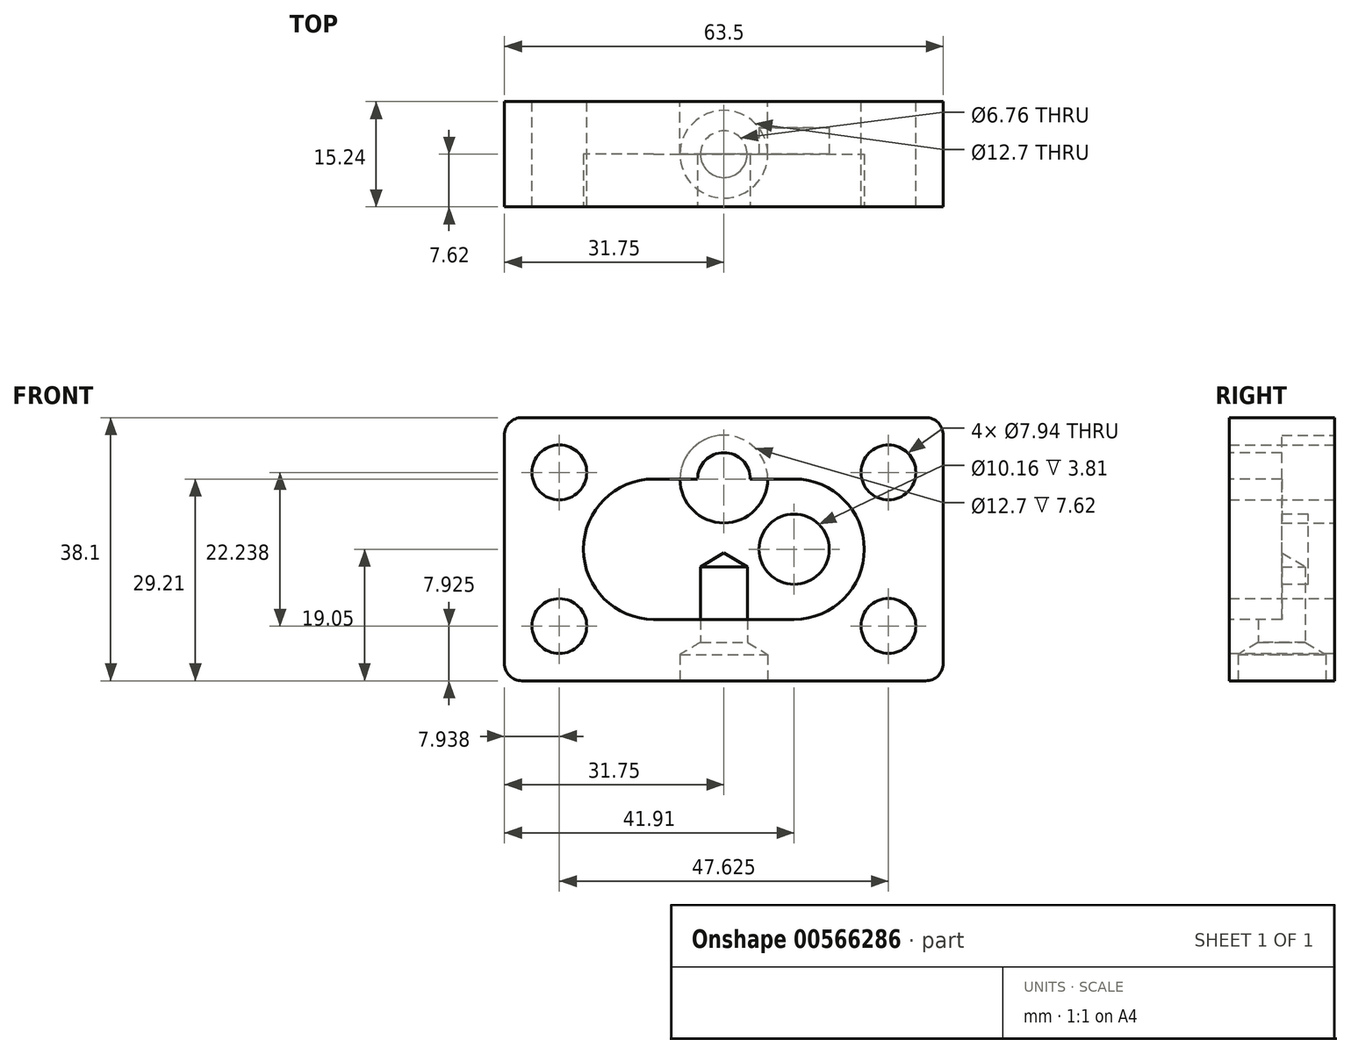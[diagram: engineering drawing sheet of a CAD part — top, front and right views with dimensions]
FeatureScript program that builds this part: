
annotation { "Feature Type Name" : "Feature", "Feature Type Description" : "" }
export const myFeature = defineFeature(function(context is Context, id is Id, definition is map)
    precondition{}
    {
        {
            var Q0;
            Q0=qCreatedBy(makeId("Front.planeOp"),FACE);
            var sketch = newSketch(context, id + "F0", { "sketchPlane" : qUnion([Q0])});
            skLineSegment(sketch, "E0.bottom", {"start": v(-31.75, 19.05) * mm, "end": v(31.75, 19.05) * mm});
            skLineSegment(sketch, "E0.top", {"start": v(-31.75, -19.05) * mm, "end": v(31.75, -19.05) * mm});
            skLineSegment(sketch, "E0.left", {"start": v(-31.75, 19.05) * mm, "end": v(-31.75, -19.05) * mm});
            skLineSegment(sketch, "E0.right", {"start": v(31.75, 19.05) * mm, "end": v(31.75, -19.05) * mm});
            skCircle(sketch, "E1", {"center": v(-23.81, 11.11) * mm, "radius": 3.97 * mm});
            skCircle(sketch, "E2", {"center": v(23.81, 11.11) * mm, "radius": 3.97 * mm});
            skCircle(sketch, "E3", {"center": v(23.81, -11.11) * mm, "radius": 3.97 * mm});
            skCircle(sketch, "E4", {"center": v(-23.81, -11.13) * mm, "radius": 3.97 * mm});
            skSolve(sketch);
        }
        {
            var Q0;
            Q0 = qSketchRegion(id + "F0", true);
            extrude(context, id + "F1", {"entities" : qUnion([Q0]), "depth" : 15.24 * mm, "offsetDistance" : 25.4 * mm});
        }
        {
            var Q0;
            Q0=makeQuery(id+"F1.opExtrude","CAP_FACE",FACE,{"disambiguationData":[OSD([sQuery(id+"F0.wireOp",EDGE,"E0.bottom"),sQuery(id+"F0.wireOp",EDGE,"E0.top"),sQuery(id+"F0.wireOp",EDGE,"E0.left"),sQuery(id+"F0.wireOp",EDGE,"E0.right"),sQuery(id+"F0.wireOp",EDGE,"E1"),sQuery(id+"F0.wireOp",EDGE,"E2"),sQuery(id+"F0.wireOp",EDGE,"E3"),sQuery(id+"F0.wireOp",EDGE,"E4")])],"isStart":false});
            var sketch = newSketch(context, id + "F2", { "sketchPlane" : qUnion([Q0])});
            skCircle(sketch, "E5", {"center": v(10.16, 0) * mm, "radius": 10.16 * mm});
            skCircle(sketch, "E6", {"center": v(-10.16, 0) * mm, "radius": 10.16 * mm});
            skLineSegment(sketch, "E7", {"start": v(-10.16, 10.16) * mm, "end": v(10.16, 10.16) * mm});
            skLineSegment(sketch, "E8", {"start": v(-10.16, -10.16) * mm, "end": v(10.16, -10.16) * mm});
            skSolve(sketch);
        }
        {
            var Q0;
            Q0 = qSketchRegion(id + "F2", true);
            extrude(context, id + "F3", {"entities" : qUnion([Q0]), "operationType" : NewBodyOperationType.REMOVE, "oppositeDirection" : true, "depth" : 7.62 * mm, "offsetDistance" : 25.4 * mm});
        }
        {
            var Q0;
            Q0=makeQuery(id+"F3.boolean.opBoolean","COPY",FACE,{"derivedFrom":makeQuery(id+"F3.opExtrude","CAP_FACE",FACE,{"disambiguationData":[OSD([sQuery(id+"F2.wireOp",EDGE,"E5"),sQuery(id+"F2.wireOp",EDGE,"E6"),sQuery(id+"F2.wireOp",EDGE,"E7"),sQuery(id+"F2.wireOp",EDGE,"E8")])],"isStart":false})});
            var sketch = newSketch(context, id + "F4", { "sketchPlane" : qUnion([Q0])});
            skCircle(sketch, "E9", {"center": v(10.16, 0) * mm, "radius": 5.08 * mm});
            skSolve(sketch);
        }
        {
            var Q0;
            Q0=makeQuery(id+"F4.imprint","IMPRINT",FACE,{"disambiguationData":[TD([[makeQuery(id+"F4.imprint","IMPRINT",EDGE,{"derivedFrom":sQuery(id+"F4.wireOp",EDGE,"E9")}),1.0]])]});
            extrude(context, id + "F5", {"entities" : qUnion([Q0]), "operationType" : NewBodyOperationType.REMOVE, "oppositeDirection" : true, "depth" : 3.8 * mm, "offsetDistance" : 25.4 * mm});
        }
        {
            var Q0;
            Q0=makeQuery(id+"F1.opExtrude","CAP_FACE",FACE,{"disambiguationData":[OSD([sQuery(id+"F0.wireOp",EDGE,"E0.bottom"),sQuery(id+"F0.wireOp",EDGE,"E0.top"),sQuery(id+"F0.wireOp",EDGE,"E0.left"),sQuery(id+"F0.wireOp",EDGE,"E0.right"),sQuery(id+"F0.wireOp",EDGE,"E1"),sQuery(id+"F0.wireOp",EDGE,"E2"),sQuery(id+"F0.wireOp",EDGE,"E3"),sQuery(id+"F0.wireOp",EDGE,"E4")])],"isStart":false});
            var sketch = newSketch(context, id + "F6", { "sketchPlane" : qUnion([Q0])});
            skCircle(sketch, "E10", {"center": v(0, 10.16) * mm, "radius": 3.81 * mm});
            skSolve(sketch);
        }
        {
            var Q0;
            {var subQ0=sQuery(id+"F6.wireOp",EDGE,"E10");var subQ1=makeQuery(id+"F3.boolean.opBoolean","COPY",EDGE,{"derivedFrom":makeQuery(id+"F3.opExtrude","CAP_EDGE",EDGE,{"disambiguationData":[OSD([sQuery(id+"F2.wireOp",EDGE,"E7")])],"isStart":true})});var subQ2=makeQuery(id+"F6.imprint","INTERSECT",VERTEX,{"disambiguationData":[OD(0.0)],"derivedFrom":[subQ1,subQ0]});Q0=makeQuery(id+"F6.imprint","IMPRINT",FACE,{"disambiguationData":[TD([[makeQuery(id+"F6.imprint","IMPRINT",EDGE,{"disambiguationData":[TD([[subQ2,-1.0]])],"derivedFrom":subQ0}),1.0]])]});}
            var Q1;
            {var subQ0=sQuery(id+"F6.wireOp",EDGE,"E10");var subQ1=makeQuery(id+"F3.boolean.opBoolean","COPY",EDGE,{"derivedFrom":makeQuery(id+"F3.opExtrude","CAP_EDGE",EDGE,{"disambiguationData":[OSD([sQuery(id+"F2.wireOp",EDGE,"E7")])],"isStart":true})});var subQ2=makeQuery(id+"F6.imprint","INTERSECT",VERTEX,{"disambiguationData":[OD(0.0)],"derivedFrom":[subQ1,subQ0]});Q1=makeQuery(id+"F6.imprint","IMPRINT",FACE,{"disambiguationData":[TD([[makeQuery(id+"F6.imprint","IMPRINT",EDGE,{"disambiguationData":[TD([[subQ2,1.0]])],"derivedFrom":subQ0}),1.0]])]});}
            extrude(context, id + "F7", {"entities" : qUnion([Q0, Q1]), "operationType" : NewBodyOperationType.REMOVE, "oppositeDirection" : true, "depth" : 25.4 * mm, "offsetDistance" : 25.4 * mm});
        }
        {
            var Q0;
            Q0=makeQuery(id+"F1.opExtrude","CAP_FACE",FACE,{"disambiguationData":[OSD([sQuery(id+"F0.wireOp",EDGE,"E0.bottom"),sQuery(id+"F0.wireOp",EDGE,"E0.top"),sQuery(id+"F0.wireOp",EDGE,"E0.left"),sQuery(id+"F0.wireOp",EDGE,"E0.right"),sQuery(id+"F0.wireOp",EDGE,"E1"),sQuery(id+"F0.wireOp",EDGE,"E2"),sQuery(id+"F0.wireOp",EDGE,"E3"),sQuery(id+"F0.wireOp",EDGE,"E4")])],"isStart":true});
            var sketch = newSketch(context, id + "F8", { "sketchPlane" : qUnion([Q0])});
            skCircle(sketch, "E11", {"center": v(0, 10.16) * mm, "radius": 6.35 * mm});
            skSolve(sketch);
        }
        {
            var Q0;
            Q0=makeQuery(id+"F8.imprint","IMPRINT",FACE,{"disambiguationData":[TD([[makeQuery(id+"F8.imprint","IMPRINT",EDGE,{"derivedFrom":sQuery(id+"F8.wireOp",EDGE,"E11")}),1.0]])]});
            extrude(context, id + "F9", {"entities" : qUnion([Q0]), "operationType" : NewBodyOperationType.REMOVE, "oppositeDirection" : true, "depth" : 7.62 * mm, "offsetDistance" : 25.4 * mm});
        }
        {
            var Q0;
            Q0=makeQuery(id+"F1.opExtrude","SWEPT_FACE",FACE,{"disambiguationData":[OSD([sQuery(id+"F0.wireOp",EDGE,"E0.top")])]});
            var sketch = newSketch(context, id + "F10", { "sketchPlane" : qUnion([Q0])});
            skPoint(sketch, "E12", {"position": v(0, 7.62) * mm});
            skSolve(sketch);
        }
        {
            var Q0;
            Q0=sQuery(id+"F10.wireOp",VERTEX,"E12");
            var Q1;
            Q1=makeQuery(id+"F1.opExtrude","SWEPT_BODY",BODY,{"disambiguationData":[OSD([sQuery(id+"F0.wireOp",EDGE,"E0.bottom"),sQuery(id+"F0.wireOp",EDGE,"E0.top"),sQuery(id+"F0.wireOp",EDGE,"E0.left"),sQuery(id+"F0.wireOp",EDGE,"E0.right"),sQuery(id+"F0.wireOp",EDGE,"E1"),sQuery(id+"F0.wireOp",EDGE,"E2"),sQuery(id+"F0.wireOp",EDGE,"E3"),sQuery(id+"F0.wireOp",EDGE,"E4")])]});
            hole(context, id + "F11", {"style" : HoleStyle.SIMPLE, "endStyle" : HoleEndStyle.BLIND, "standardTappedOrClearance" : lookupTablePath({ "standard" : "ANSI", "fit" : "Normal (ASME)", "engagement" : "75%", "pitch" : "20 tpi", "size" : "1/4", "type" : "Clearance" }), "standardBlindInLast" : lookupTablePath({ "fit" : "Free", "standard" : "ANSI", "engagement" : "75%", "pitch" : "20 tpi", "size" : "1/4", "type" : "Clearance" }), "holeDiameter" : 6.76 * mm, "showTappedDepth" : true, "holeDepth" : 16.51 * mm, "isTappedThrough" : true, "tappedDepth" : 12.7 * mm, "tapClearance" : 3, "locations" : qUnion([Q0]), "scope" : qUnion([Q1]), "majorDiameter" : 6.35 * mm});
        }
        {
            var Q0;
            Q0=makeQuery(id+"F1.opExtrude","SWEPT_FACE",FACE,{"disambiguationData":[OSD([sQuery(id+"F0.wireOp",EDGE,"E0.top")])]});
            var sketch = newSketch(context, id + "F12", { "sketchPlane" : qUnion([Q0])});
            skPoint(sketch, "E13", {"position": v(0, 7.62) * mm});
            skSolve(sketch);
        }
        {
            var Q0;
            Q0=sQuery(id+"F12.wireOp",VERTEX,"E13");
            var Q1;
            Q1=makeQuery(id+"F1.opExtrude","SWEPT_BODY",BODY,{"disambiguationData":[OSD([sQuery(id+"F0.wireOp",EDGE,"E0.bottom"),sQuery(id+"F0.wireOp",EDGE,"E0.top"),sQuery(id+"F0.wireOp",EDGE,"E0.left"),sQuery(id+"F0.wireOp",EDGE,"E0.right"),sQuery(id+"F0.wireOp",EDGE,"E1"),sQuery(id+"F0.wireOp",EDGE,"E2"),sQuery(id+"F0.wireOp",EDGE,"E3"),sQuery(id+"F0.wireOp",EDGE,"E4")])]});
            hole(context, id + "F13", {"style" : HoleStyle.SIMPLE, "endStyle" : HoleEndStyle.BLIND, "holeDiameter" : 12.7 * mm, "holeDepth" : 3.8 * mm, "isTappedThrough" : true, "tappedDepth" : 12.7 * mm, "tapClearance" : 3, "locations" : qUnion([Q0]), "scope" : qUnion([Q1])});
        }
        {
            var Q0;
            Q0=makeQuery(id+"F1.opExtrude","SWEPT_EDGE",EDGE,{"disambiguationData":[OSD([sQuery(id+"F0.wireOp",EDGE,"E0.top"),sQuery(id+"F0.wireOp",EDGE,"E0.right")])]});
            var Q1;
            Q1=makeQuery(id+"F1.opExtrude","SWEPT_EDGE",EDGE,{"disambiguationData":[OSD([sQuery(id+"F0.wireOp",EDGE,"E0.top"),sQuery(id+"F0.wireOp",EDGE,"E0.left")])]});
            var Q2;
            Q2=makeQuery(id+"F1.opExtrude","SWEPT_EDGE",EDGE,{"disambiguationData":[OSD([sQuery(id+"F0.wireOp",EDGE,"E0.bottom"),sQuery(id+"F0.wireOp",EDGE,"E0.right")])]});
            var Q3;
            Q3=makeQuery(id+"F1.opExtrude","SWEPT_EDGE",EDGE,{"disambiguationData":[OSD([sQuery(id+"F0.wireOp",EDGE,"E0.bottom"),sQuery(id+"F0.wireOp",EDGE,"E0.left")])]});
            fillet(context, id + "F14", {"entities" : qUnion([Q0, Q1, Q2, Q3]), "radius" : 2.54 * mm, "tangentPropagation" : true, "allowEdgeOverflow" : false});
        }
    });
